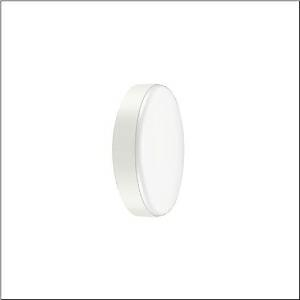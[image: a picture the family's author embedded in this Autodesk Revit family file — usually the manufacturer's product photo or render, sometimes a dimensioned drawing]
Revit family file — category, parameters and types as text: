
# Revit family: rondel_31_51wc10ma42as
name_source: partatom
category: Lighting Fixtures
units: mm (PartAtom-declared; Revit-internal decimal feet)

## family parameters
Cut with Voids When Loaded = No
Host = Face
Light Source = No
Part Type = Normal
Room Calculation Point = No
Round Connector Dimension = Use Diameter
Shared = No

## types (1)
- --- (1 x LED, 2550 lm, 20.5 W, 4000K)
    Apparent Load = 21 VA
    CIE Flux Codes = 44 75 94 94 100
    Color Rendering = 80
    Color Temperature = 4000K
    Default Elevation = 1800 mm
    Description = Rondel 31, wall and ceiling luminaire, primary optical cover: cover, of PC, opal, light emission: direct distribution, primary light characteristic: symmetric, installation type: surface-mounted, LED, rated luminous flux: 2.400lm, luminous efficacy: 117lm/W, light colour: 840, colour temperature: 4000K, with terminal, 3-pole, max. 2.5mm², mains connection: 220..240V, AC, 50/60Hz, rated input power: 20.5W, luminaire housing, of PC, traffic white (RAL 9016), diameter: 350mm, brightness and presence sensor, HF sensor, protection rating (complete): IP65, insulation class (complete): insulation class II (safety insulation), certification: CE, impact resistance: IK10, permissible storage temperature: -20..+60°C, packaging unit: 1 piece
    Height = 97 mm
    Lamp = 1 x LED
    Lamp Light Flux = 2550 lm
    Lamp Power = 20.5 W
    Lamp count = 1
    Length = 350 mm
    Luminous efficacy = 124 lm/W
    Manufacturer = Siteco
    ModVariant = No
    Model = 51WC10MA42AS
    Mounting Place = Ceiling
    Mounting Type = Surface mounted
    Number of Poles = 1
    OnlyDefault = Yes
    Power Factor = 1
    Product Name = Rondel 31
    Product group = wall and ceiling luminaire
    ProductGroupID = 301
    Protection Class = Protection class II
    Protection Degree = IP 65
    RLX_Detail_Level = 1
    RlxData = <blob elided: 30437 chars, md5=dce8db8e>
    Socket = socket
    Standby Power = 0 W
    System Light Flux = 2550 lm
    System Power = 21 W
    Type Comments = factory setting: luminous flux: 100 % | (ON | ON)
    Type Image = l_1007027.jpg
    URL = http://relux.com
    VarID = @adj_060561
    Voltage = 0 V
    Weight = 0.00 kg
    Width = 0 mm  [stored 0 ft]

note: [stored X ft] marks values corroborated as IEEE doubles in the binary element streams (Revit-internal decimal feet)

## geometry (parser evidence)
native form markers: Blend x4, Sweep x13
no freeform markers — native parametric forms only
